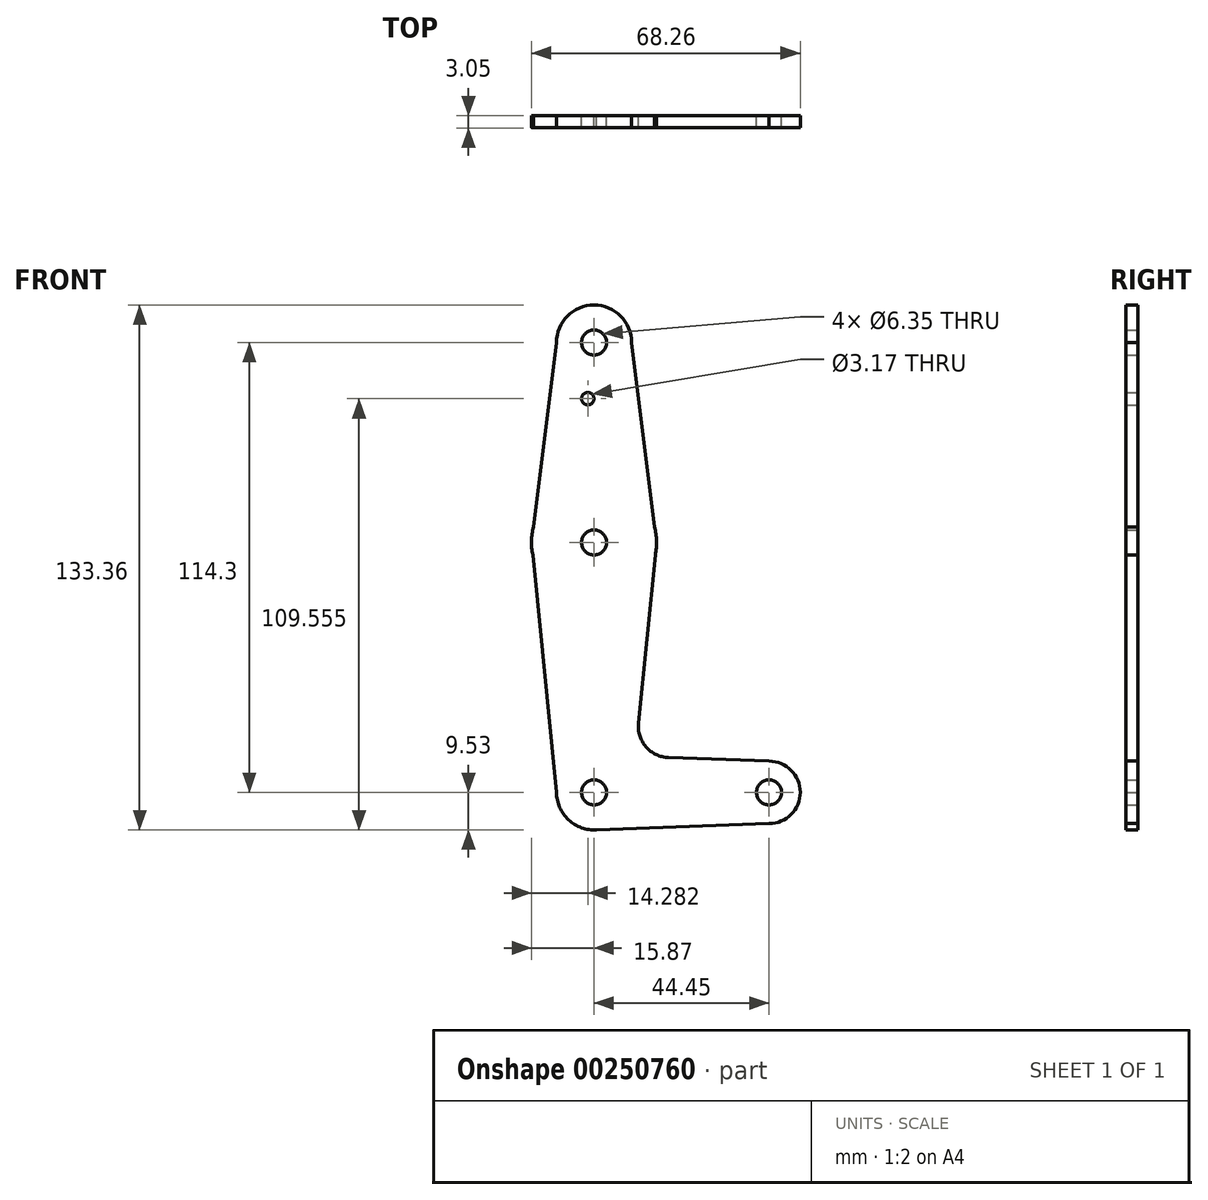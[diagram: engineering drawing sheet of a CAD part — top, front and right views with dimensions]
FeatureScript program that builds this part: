
annotation { "Feature Type Name" : "Feature", "Feature Type Description" : "" }
export const myFeature = defineFeature(function(context is Context, id is Id, definition is map)
    precondition{}
    {
        {
            var Q0;
            Q0=qCreatedBy(makeId("Front.planeOp"),FACE);
            var sketch = newSketch(context, id + "F0", { "sketchPlane" : qUnion([Q0])});
            skLineSegment(sketch, "E0", {"start": v(0, 0) * mm, "end": v(0, 114.3) * mm, "construction": true});
            skLineSegment(sketch, "E1", {"start": v(0, 0) * mm, "end": v(44.45, 0) * mm, "construction": true});
            skCircle(sketch, "E2", {"center": v(0, 114.3) * mm, "radius": 9.53 * mm});
            skCircle(sketch, "E3", {"center": v(0, 63.5) * mm, "radius": 15.88 * mm});
            skCircle(sketch, "E4", {"center": v(44.45, 0) * mm, "radius": 7.94 * mm});
            skCircle(sketch, "E5", {"center": v(0, 0) * mm, "radius": 9.53 * mm});
            skLineSegment(sketch, "E6", {"start": v(9.52, 114.3) * mm, "end": v(15.88, 63.5) * mm});
            skLineSegment(sketch, "E7", {"start": v(15.88, 63.5) * mm, "end": v(11.28, 17.59) * mm});
            skLineSegment(sketch, "E8", {"start": v(0, -9.52) * mm, "end": v(44.45, -7.94) * mm});
            skLineSegment(sketch, "E9", {"start": v(18.91, 8.85) * mm, "end": v(44.45, 7.94) * mm});
            skLineSegment(sketch, "E10", {"start": v(-9.52, 114.3) * mm, "end": v(-15.88, 63.5) * mm});
            skLineSegment(sketch, "E11", {"start": v(-15.88, 63.5) * mm, "end": v(-9.52, 0) * mm});
            skCircle(sketch, "E12", {"center": v(0, 114.3) * mm, "radius": 3.18 * mm});
            skCircle(sketch, "E13", {"center": v(0, 63.5) * mm, "radius": 3.18 * mm});
            skCircle(sketch, "E14", {"center": v(0, 0) * mm, "radius": 3.18 * mm});
            skCircle(sketch, "E15", {"center": v(44.45, 0) * mm, "radius": 3.18 * mm});
            skArc(sketch, "E16.filletArc", {"start": v(11.28, 17.59) * mm, "mid": v(13.2, 11.57) * mm, "end": v(18.91, 8.85) * mm});
            skCircle(sketch, "E17", {"center": v(-1.59, 100.03) * mm, "radius": 1.59 * mm});
            skSolve(sketch);
        }
        {
            var Q0;
            Q0 = qSketchRegion(id + "F0", true);
            extrude(context, id + "F1", {"entities" : qUnion([Q0]), "depth" : 3.05 * mm});
        }
    });
